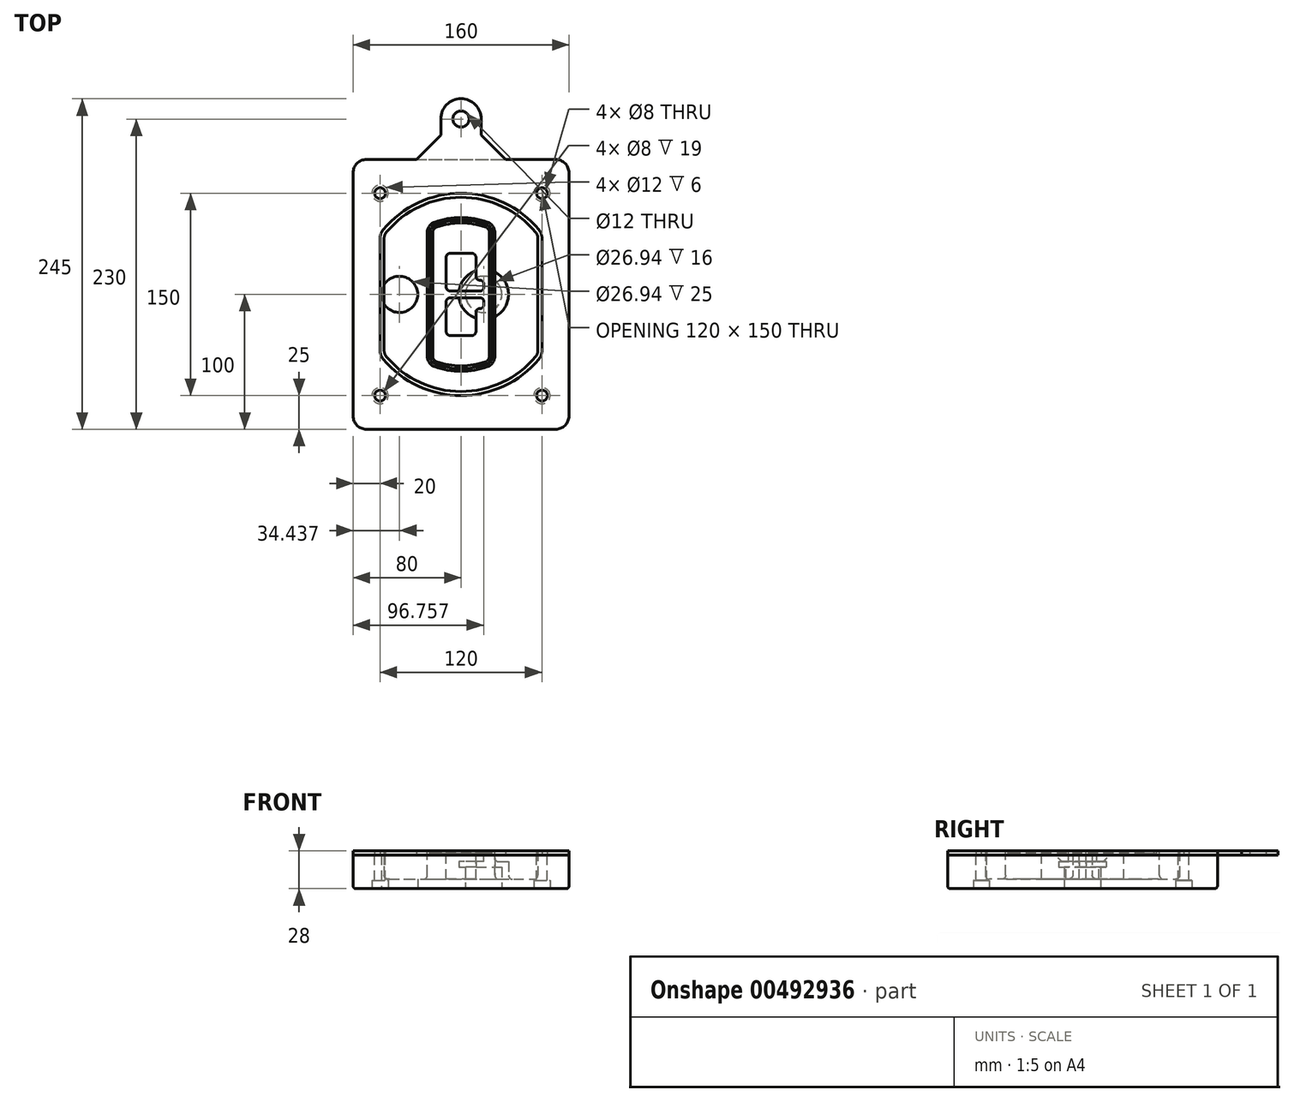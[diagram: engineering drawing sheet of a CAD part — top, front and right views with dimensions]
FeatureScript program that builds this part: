
annotation { "Feature Type Name" : "Feature", "Feature Type Description" : "" }
export const myFeature = defineFeature(function(context is Context, id is Id, definition is map)
    precondition{}
    {
        {
            var Q0;
            Q0=qCreatedBy(makeId("Top.planeOp"),FACE);
            var sketch = newSketch(context, id + "F0", { "sketchPlane" : qUnion([Q0])});
            skPoint(sketch, "E0.rect.middle", {"position": v(0, 0) * mm});
            skLineSegment(sketch, "E1.bottom", {"start": v(-70, -100) * mm, "end": v(70, -100) * mm});
            skLineSegment(sketch, "E1.top", {"start": v(-70, 100) * mm, "end": v(70, 100) * mm});
            skLineSegment(sketch, "E1.left", {"start": v(-80, -90) * mm, "end": v(-80, 90) * mm});
            skLineSegment(sketch, "E1.right", {"start": v(80, -90) * mm, "end": v(80, 90) * mm});
            skLineSegment(sketch, "E2", {"start": v(-80, 100) * mm, "end": v(80, -100) * mm, "construction": true});
            skLineSegment(sketch, "E3", {"start": v(80, 100) * mm, "end": v(-80, -100) * mm, "construction": true});
            skCircle(sketch, "E4", {"center": v(-60, 75) * mm, "radius": 4 * mm});
            skCircle(sketch, "E5", {"center": v(60, 75) * mm, "radius": 4 * mm});
            skCircle(sketch, "E6", {"center": v(60, -75) * mm, "radius": 4 * mm});
            skCircle(sketch, "E7", {"center": v(-60, -75) * mm, "radius": 4 * mm});
            skLineSegment(sketch, "E8", {"start": v(-60, 75) * mm, "end": v(60, 75) * mm, "construction": true});
            skLineSegment(sketch, "E9", {"start": v(60, 75) * mm, "end": v(60, -75) * mm, "construction": true});
            skLineSegment(sketch, "E10", {"start": v(60, -75) * mm, "end": v(-60, -75) * mm, "construction": true});
            skLineSegment(sketch, "E11", {"start": v(-60, -75) * mm, "end": v(-60, 75) * mm, "construction": true});
            skLineSegment(sketch, "E12", {"start": v(-60, 41.53) * mm, "end": v(-60, -41.53) * mm});
            skLineSegment(sketch, "E13", {"start": v(60, 41.53) * mm, "end": v(60, -41.53) * mm});
            skArc(sketch, "E14", {"start": v(57.7, 47.92) * mm, "mid": v(0, 75) * mm, "end": v(-57.7, 47.92) * mm});
            skArc(sketch, "E15", {"start": v(-57.7, -47.92) * mm, "mid": v(0, -75) * mm, "end": v(57.7, -47.92) * mm});
            skLineSegment(sketch, "E16", {"start": v(-60, 0) * mm, "end": v(60, 0) * mm, "construction": true});
            skPoint(sketch, "E17.visualSharp", {"position": v(-60, -45) * mm});
            skArc(sketch, "E17.filletArc", {"start": v(-60, -41.53) * mm, "mid": v(-59.4, -44.93) * mm, "end": v(-57.7, -47.92) * mm});
            skPoint(sketch, "E18.visualSharp", {"position": v(-60, 45) * mm});
            skArc(sketch, "E18.filletArc", {"start": v(-57.7, 47.92) * mm, "mid": v(-59.4, 44.93) * mm, "end": v(-60, 41.53) * mm});
            skPoint(sketch, "E19.visualSharp", {"position": v(60, 45) * mm});
            skArc(sketch, "E19.filletArc", {"start": v(60, 41.53) * mm, "mid": v(59.4, 44.93) * mm, "end": v(57.7, 47.92) * mm});
            skPoint(sketch, "E20.visualSharp", {"position": v(60, -45) * mm});
            skArc(sketch, "E20.filletArc", {"start": v(57.7, -47.92) * mm, "mid": v(59.4, -44.93) * mm, "end": v(60, -41.53) * mm});
            skPoint(sketch, "E21.visualSharp", {"position": v(-80, 100) * mm});
            skArc(sketch, "E21.filletArc", {"start": v(-70, 100) * mm, "mid": v(-77.07, 97.07) * mm, "end": v(-80, 90) * mm});
            skPoint(sketch, "E22.visualSharp", {"position": v(80, 100) * mm});
            skArc(sketch, "E22.filletArc", {"start": v(80, 90) * mm, "mid": v(77.07, 97.07) * mm, "end": v(70, 100) * mm});
            skPoint(sketch, "E23.visualSharp", {"position": v(80, -100) * mm});
            skArc(sketch, "E23.filletArc", {"start": v(70, -100) * mm, "mid": v(77.07, -97.07) * mm, "end": v(80, -90) * mm});
            skPoint(sketch, "E24.visualSharp", {"position": v(-80, -100) * mm});
            skArc(sketch, "E24.filletArc", {"start": v(-80, -90) * mm, "mid": v(-77.07, -97.07) * mm, "end": v(-70, -100) * mm});
            skArc(sketch, "E25.0", {"start": v(57, 41.53) * mm, "mid": v(56.58, 43.91) * mm, "end": v(55.38, 46) * mm});
            skLineSegment(sketch, "E25.1", {"start": v(57, 41.53) * mm, "end": v(57, -41.53) * mm});
            skArc(sketch, "E25.2", {"start": v(55.38, -46) * mm, "mid": v(56.58, -43.91) * mm, "end": v(57, -41.53) * mm});
            skArc(sketch, "E25.3", {"start": v(-55.38, -46) * mm, "mid": v(0, -72) * mm, "end": v(55.38, -46) * mm});
            skArc(sketch, "E25.4", {"start": v(-57, -41.53) * mm, "mid": v(-56.58, -43.91) * mm, "end": v(-55.38, -46) * mm});
            skArc(sketch, "E25.5", {"start": v(55.38, 46) * mm, "mid": v(0, 72) * mm, "end": v(-55.38, 46) * mm});
            skLineSegment(sketch, "E25.6", {"start": v(-57, 41.53) * mm, "end": v(-57, -41.53) * mm});
            skArc(sketch, "E25.7", {"start": v(-55.38, 46) * mm, "mid": v(-56.58, 43.91) * mm, "end": v(-57, 41.53) * mm});
            skArc(sketch, "E26.0", {"start": v(-60.77, 50.48) * mm, "mid": v(-63.17, 46.29) * mm, "end": v(-64, 41.53) * mm});
            skArc(sketch, "E26.1", {"start": v(60.77, 50.48) * mm, "mid": v(0, 79) * mm, "end": v(-60.77, 50.48) * mm});
            skArc(sketch, "E26.2", {"start": v(64, 41.53) * mm, "mid": v(63.17, 46.29) * mm, "end": v(60.77, 50.48) * mm});
            skLineSegment(sketch, "E26.3", {"start": v(64, 41.53) * mm, "end": v(64, -41.53) * mm});
            skArc(sketch, "E26.4", {"start": v(60.77, -50.48) * mm, "mid": v(63.17, -46.29) * mm, "end": v(64, -41.53) * mm});
            skLineSegment(sketch, "E26.5", {"start": v(-64, 41.53) * mm, "end": v(-64, -41.53) * mm});
            skArc(sketch, "E26.6", {"start": v(-60.77, -50.48) * mm, "mid": v(0, -79) * mm, "end": v(60.77, -50.48) * mm});
            skArc(sketch, "E26.7", {"start": v(-64, -41.53) * mm, "mid": v(-63.17, -46.29) * mm, "end": v(-60.77, -50.48) * mm});
            skSolve(sketch);
        }
        {
            var Q0;
            Q0=makeQuery(id+"F0.imprint","IMPRINT",FACE,{"disambiguationData":[TD([[makeQuery(id+"F0.imprint","IMPRINT",EDGE,{"derivedFrom":sQuery(id+"F0.wireOp",EDGE,"E1.bottom")}),1.0]])]});
            var Q1;
            Q1=makeQuery(id+"F0.imprint","IMPRINT",FACE,{"disambiguationData":[TD([[makeQuery(id+"F0.imprint","IMPRINT",EDGE,{"derivedFrom":sQuery(id+"F0.wireOp",EDGE,"E12")}),1.0]])]});
            var Q2;
            Q2=makeQuery(id+"F0.imprint","IMPRINT",FACE,{"disambiguationData":[TD([[makeQuery(id+"F0.imprint","IMPRINT",EDGE,{"derivedFrom":sQuery(id+"F0.wireOp",EDGE,"E25.0")}),1.0]])]});
            var Q3;
            Q3=makeQuery(id+"F0.imprint","IMPRINT",FACE,{"disambiguationData":[TD([[makeQuery(id+"F0.imprint","IMPRINT",EDGE,{"derivedFrom":sQuery(id+"F0.wireOp",EDGE,"E12")}),-1.0]])]});
            extrude(context, id + "F1", {"entities" : qUnion([Q0, Q1, Q2, Q3]), "oppositeDirection" : true, "depth" : 25 * mm});
        }
        {
            var Q0;
            Q0=makeQuery(id+"F0.imprint","IMPRINT",FACE,{"disambiguationData":[TD([[makeQuery(id+"F0.imprint","IMPRINT",EDGE,{"derivedFrom":sQuery(id+"F0.wireOp",EDGE,"E12")}),1.0]])]});
            extrude(context, id + "F2", {"entities" : qUnion([Q0]), "operationType" : NewBodyOperationType.ADD, "depth" : 3 * mm});
        }
        {
            var Q0;
            Q0=makeQuery(id+"F0.imprint","IMPRINT",FACE,{"disambiguationData":[TD([[makeQuery(id+"F0.imprint","IMPRINT",EDGE,{"derivedFrom":sQuery(id+"F0.wireOp",EDGE,"E25.0")}),1.0]])]});
            extrude(context, id + "F3", {"entities" : qUnion([Q0]), "operationType" : NewBodyOperationType.REMOVE, "oppositeDirection" : true, "depth" : 18 * mm});
        }
        {
            var Q0;
            Q0=makeQuery(id+"F2.opExtrude","CAP_FACE",FACE,{"disambiguationData":[OSD([sQuery(id+"F0.wireOp",EDGE,"E12"),sQuery(id+"F0.wireOp",EDGE,"E13"),sQuery(id+"F0.wireOp",EDGE,"E14"),sQuery(id+"F0.wireOp",EDGE,"E15"),sQuery(id+"F0.wireOp",EDGE,"E17.filletArc"),sQuery(id+"F0.wireOp",EDGE,"E18.filletArc"),sQuery(id+"F0.wireOp",EDGE,"E19.filletArc"),sQuery(id+"F0.wireOp",EDGE,"E20.filletArc"),sQuery(id+"F0.wireOp",EDGE,"E25.0"),sQuery(id+"F0.wireOp",EDGE,"E25.1"),sQuery(id+"F0.wireOp",EDGE,"E25.2"),sQuery(id+"F0.wireOp",EDGE,"E25.3"),sQuery(id+"F0.wireOp",EDGE,"E25.4"),sQuery(id+"F0.wireOp",EDGE,"E25.5"),sQuery(id+"F0.wireOp",EDGE,"E25.6"),sQuery(id+"F0.wireOp",EDGE,"E25.7")])],"isStart":false});
            var sketch = newSketch(context, id + "F4", { "sketchPlane" : qUnion([Q0])});
            skArc(sketch, "E27.0", {"start": v(-19.78, -53.46) * mm, "mid": v(0, -57) * mm, "end": v(19.78, -53.46) * mm});
            skArc(sketch, "E28.0", {"start": v(19.78, 53.46) * mm, "mid": v(0, 57) * mm, "end": v(-19.78, 53.46) * mm});
            skLineSegment(sketch, "E29", {"start": v(-25, 45.96) * mm, "end": v(-25, -45.96) * mm});
            skLineSegment(sketch, "E30", {"start": v(25, 45.96) * mm, "end": v(25, -45.96) * mm});
            skLineSegment(sketch, "E31", {"start": v(-25, 51.22) * mm, "end": v(25, 51.22) * mm, "construction": true});
            skLineSegment(sketch, "E32", {"start": v(-25, -51.22) * mm, "end": v(25, -51.22) * mm, "construction": true});
            skPoint(sketch, "E33.visualSharp", {"position": v(-25, 51.22) * mm});
            skArc(sketch, "E33.filletArc", {"start": v(-19.78, 53.46) * mm, "mid": v(-23.57, 50.53) * mm, "end": v(-25, 45.96) * mm});
            skPoint(sketch, "E34.visualSharp", {"position": v(25, 51.22) * mm});
            skArc(sketch, "E34.filletArc", {"start": v(25, 45.96) * mm, "mid": v(23.57, 50.53) * mm, "end": v(19.78, 53.46) * mm});
            skPoint(sketch, "E35.visualSharp", {"position": v(25, -51.22) * mm});
            skArc(sketch, "E35.filletArc", {"start": v(19.78, -53.46) * mm, "mid": v(23.57, -50.53) * mm, "end": v(25, -45.96) * mm});
            skPoint(sketch, "E36.visualSharp", {"position": v(-25, -51.22) * mm});
            skArc(sketch, "E36.filletArc", {"start": v(-25, -45.96) * mm, "mid": v(-23.57, -50.53) * mm, "end": v(-19.78, -53.46) * mm});
            skArc(sketch, "E37.0", {"start": v(55.38, 46) * mm, "mid": v(0, 72) * mm, "end": v(-55.38, 46) * mm});
            skArc(sketch, "E37.1", {"start": v(-55.38, 46) * mm, "mid": v(-56.58, 43.91) * mm, "end": v(-57, 41.53) * mm});
            skLineSegment(sketch, "E37.2", {"start": v(-57, 41.53) * mm, "end": v(-57, -41.53) * mm});
            skArc(sketch, "E37.3", {"start": v(-57, -41.53) * mm, "mid": v(-56.58, -43.91) * mm, "end": v(-55.38, -46) * mm});
            skArc(sketch, "E37.4", {"start": v(-55.38, -46) * mm, "mid": v(0, -72) * mm, "end": v(55.38, -46) * mm});
            skArc(sketch, "E37.5", {"start": v(55.38, -46) * mm, "mid": v(56.58, -43.91) * mm, "end": v(57, -41.53) * mm});
            skLineSegment(sketch, "E37.6", {"start": v(57, 41.53) * mm, "end": v(57, -41.53) * mm});
            skArc(sketch, "E37.7", {"start": v(57, 41.53) * mm, "mid": v(56.58, 43.91) * mm, "end": v(55.38, 46) * mm});
            skLineSegment(sketch, "E38.0", {"start": v(23, 45.96) * mm, "end": v(23, -45.96) * mm});
            skArc(sketch, "E38.1", {"start": v(19.08, -51.58) * mm, "mid": v(21.92, -49.39) * mm, "end": v(23, -45.96) * mm});
            skArc(sketch, "E38.2", {"start": v(-19.08, -51.58) * mm, "mid": v(0, -55) * mm, "end": v(19.08, -51.58) * mm});
            skArc(sketch, "E38.3", {"start": v(-23, -45.96) * mm, "mid": v(-21.92, -49.39) * mm, "end": v(-19.08, -51.58) * mm});
            skLineSegment(sketch, "E38.4", {"start": v(-23, 45.96) * mm, "end": v(-23, -45.96) * mm});
            skArc(sketch, "E38.5", {"start": v(23, 45.96) * mm, "mid": v(21.92, 49.39) * mm, "end": v(19.08, 51.58) * mm});
            skArc(sketch, "E38.6", {"start": v(-19.08, 51.58) * mm, "mid": v(-21.92, 49.39) * mm, "end": v(-23, 45.96) * mm});
            skArc(sketch, "E38.7", {"start": v(19.08, 51.58) * mm, "mid": v(0, 55) * mm, "end": v(-19.08, 51.58) * mm});
            skArc(sketch, "E39.0", {"start": v(21, 45.96) * mm, "mid": v(20.28, 48.24) * mm, "end": v(18.39, 49.7) * mm});
            skLineSegment(sketch, "E39.1", {"start": v(21, 45.96) * mm, "end": v(21, -45.96) * mm});
            skArc(sketch, "E39.2", {"start": v(18.39, -49.7) * mm, "mid": v(20.28, -48.24) * mm, "end": v(21, -45.96) * mm});
            skArc(sketch, "E39.3", {"start": v(-18.39, -49.7) * mm, "mid": v(0, -53) * mm, "end": v(18.39, -49.7) * mm});
            skArc(sketch, "E39.4", {"start": v(-21, -45.96) * mm, "mid": v(-20.28, -48.24) * mm, "end": v(-18.39, -49.7) * mm});
            skArc(sketch, "E39.5", {"start": v(18.39, 49.7) * mm, "mid": v(0, 53) * mm, "end": v(-18.39, 49.7) * mm});
            skLineSegment(sketch, "E39.6", {"start": v(-21, 45.96) * mm, "end": v(-21, -45.96) * mm});
            skArc(sketch, "E39.7", {"start": v(-18.39, 49.7) * mm, "mid": v(-20.28, 48.24) * mm, "end": v(-21, 45.96) * mm});
            skLineSegment(sketch, "E40", {"start": v(-25, 0) * mm, "end": v(25, 0) * mm, "construction": true});
            skLineSegment(sketch, "E41", {"start": v(-11, 5.5) * mm, "end": v(-11, 27.5) * mm});
            skLineSegment(sketch, "E42", {"start": v(-8, 30.5) * mm, "end": v(8, 30.5) * mm});
            skLineSegment(sketch, "E43", {"start": v(11, 27.5) * mm, "end": v(11, 13.5) * mm});
            skLineSegment(sketch, "E44", {"start": v(14, 10.5) * mm, "end": v(14, 10.5) * mm});
            skLineSegment(sketch, "E45", {"start": v(17, 7.5) * mm, "end": v(17, 5.5) * mm});
            skLineSegment(sketch, "E46", {"start": v(14, 2.5) * mm, "end": v(-8, 2.5) * mm});
            skPoint(sketch, "E47.visualSharp", {"position": v(-11, 30.5) * mm});
            skArc(sketch, "E47.filletArc", {"start": v(-8, 30.5) * mm, "mid": v(-10.12, 29.62) * mm, "end": v(-11, 27.5) * mm});
            skPoint(sketch, "E48.visualSharp", {"position": v(11, 30.5) * mm});
            skArc(sketch, "E48.filletArc", {"start": v(11, 27.5) * mm, "mid": v(10.12, 29.62) * mm, "end": v(8, 30.5) * mm});
            skPoint(sketch, "E49.visualSharp", {"position": v(11, 10.5) * mm});
            skArc(sketch, "E49.filletArc", {"start": v(11, 13.5) * mm, "mid": v(11.88, 11.38) * mm, "end": v(14, 10.5) * mm});
            skPoint(sketch, "E50.visualSharp", {"position": v(17, 10.5) * mm});
            skArc(sketch, "E50.filletArc", {"start": v(17, 7.5) * mm, "mid": v(16.12, 9.62) * mm, "end": v(14, 10.5) * mm});
            skPoint(sketch, "E51.visualSharp", {"position": v(17, 2.5) * mm});
            skArc(sketch, "E51.filletArc", {"start": v(14, 2.5) * mm, "mid": v(16.12, 3.38) * mm, "end": v(17, 5.5) * mm});
            skPoint(sketch, "E52.visualSharp", {"position": v(-11, 2.5) * mm});
            skArc(sketch, "E52.filletArc", {"start": v(-11, 5.5) * mm, "mid": v(-10.12, 3.38) * mm, "end": v(-8, 2.5) * mm});
            skLineSegment(sketch, "E53.0.MirrorCS", {"start": v(14, -2.5) * mm, "end": v(-8, -2.5) * mm});
            skArc(sketch, "E54.0.MirrorCS", {"start": v(-11, -5.5) * mm, "mid": v(-10.12, -3.38) * mm, "end": v(-8, -2.5) * mm});
            skLineSegment(sketch, "E55.0.MirrorCS", {"start": v(-11, -5.5) * mm, "end": v(-11, -27.5) * mm});
            skArc(sketch, "E56.0.MirrorCS", {"start": v(-8, -30.5) * mm, "mid": v(-10.12, -29.62) * mm, "end": v(-11, -27.5) * mm});
            skLineSegment(sketch, "E57.0.MirrorCS", {"start": v(-8, -30.5) * mm, "end": v(8, -30.5) * mm});
            skArc(sketch, "E58.0.MirrorCS", {"start": v(11, -27.5) * mm, "mid": v(10.12, -29.62) * mm, "end": v(8, -30.5) * mm});
            skLineSegment(sketch, "E59.0.MirrorCS", {"start": v(11, -27.5) * mm, "end": v(11, -13.5) * mm});
            skArc(sketch, "E60.0.MirrorCS", {"start": v(11, -13.5) * mm, "mid": v(11.88, -11.38) * mm, "end": v(14, -10.5) * mm});
            skArc(sketch, "E61.0.MirrorCS", {"start": v(17, -7.5) * mm, "mid": v(16.12, -9.62) * mm, "end": v(14, -10.5) * mm});
            skLineSegment(sketch, "E62.0.MirrorCS", {"start": v(17, -7.5) * mm, "end": v(17, -5.5) * mm});
            skArc(sketch, "E63.0.MirrorCS", {"start": v(14, -2.5) * mm, "mid": v(16.12, -3.38) * mm, "end": v(17, -5.5) * mm});
            skSolve(sketch);
        }
        {
            var Q0;
            Q0=makeQuery(id+"F4.imprint","IMPRINT",FACE,{"disambiguationData":[TD([[makeQuery(id+"F4.imprint","IMPRINT",EDGE,{"derivedFrom":sQuery(id+"F4.wireOp",EDGE,"E27.0")}),1.0]])]});
            var Q1;
            Q1=makeQuery(id+"F4.imprint","IMPRINT",FACE,{"disambiguationData":[TD([[makeQuery(id+"F4.imprint","IMPRINT",EDGE,{"derivedFrom":sQuery(id+"F4.wireOp",EDGE,"E38.0")}),-1.0]])]});
            var Q2;
            Q2=makeQuery(id+"F4.imprint","IMPRINT",FACE,{"disambiguationData":[TD([[makeQuery(id+"F4.imprint","IMPRINT",EDGE,{"derivedFrom":sQuery(id+"F4.wireOp",EDGE,"E39.0")}),1.0]])]});
            extrude(context, id + "F5", {"entities" : qUnion([Q0, Q1, Q2]), "operationType" : NewBodyOperationType.ADD, "endBound" : BoundingType.UP_TO_NEXT, "oppositeDirection" : true, "depth" : 25 * mm});
        }
        {
            var Q0;
            Q0=makeQuery(id+"F4.imprint","IMPRINT",FACE,{"disambiguationData":[TD([[makeQuery(id+"F4.imprint","IMPRINT",EDGE,{"derivedFrom":sQuery(id+"F4.wireOp",EDGE,"E38.0")}),-1.0]])]});
            extrude(context, id + "F6", {"entities" : qUnion([Q0]), "operationType" : NewBodyOperationType.REMOVE, "oppositeDirection" : true, "depth" : 2 * mm});
        }
        {
            var Q0;
            Q0=makeQuery(id+"F1.opExtrude","CAP_FACE",FACE,{"disambiguationData":[OSD([sQuery(id+"F0.wireOp",EDGE,"E1.bottom"),sQuery(id+"F0.wireOp",EDGE,"E1.top"),sQuery(id+"F0.wireOp",EDGE,"E1.left"),sQuery(id+"F0.wireOp",EDGE,"E1.right"),sQuery(id+"F0.wireOp",EDGE,"E4"),sQuery(id+"F0.wireOp",EDGE,"E5"),sQuery(id+"F0.wireOp",EDGE,"E6"),sQuery(id+"F0.wireOp",EDGE,"E7"),sQuery(id+"F0.wireOp",EDGE,"E21.filletArc"),sQuery(id+"F0.wireOp",EDGE,"E22.filletArc"),sQuery(id+"F0.wireOp",EDGE,"E23.filletArc"),sQuery(id+"F0.wireOp",EDGE,"E24.filletArc")])],"isStart":false});
            var sketch = newSketch(context, id + "F7", { "sketchPlane" : qUnion([Q0])});
            skCircle(sketch, "E64", {"center": v(16.76, 0) * mm, "radius": 13.47 * mm});
            skCircle(sketch, "E65", {"center": v(-45.56, 0) * mm, "radius": 13.47 * mm});
            skLineSegment(sketch, "E66", {"start": v(80, 0) * mm, "end": v(-80, 0) * mm});
            skCircle(sketch, "E67", {"center": v(16.76, 0) * mm, "radius": 18.47 * mm});
            skCircle(sketch, "E68", {"center": v(60, -75) * mm, "radius": 6 * mm});
            skCircle(sketch, "E69", {"center": v(-60, -75) * mm, "radius": 6 * mm});
            skCircle(sketch, "E70", {"center": v(-60, 75) * mm, "radius": 6 * mm});
            skCircle(sketch, "E71", {"center": v(60, 75) * mm, "radius": 6 * mm});
            skSolve(sketch);
        }
        {
            var Q0;
            {var subQ1=sQuery(id+"F7.wireOp",EDGE,"E66");var subQ4=sQuery(id+"F7.wireOp",EDGE,"E64");var subQ6=makeQuery(id+"F7.imprint","INTERSECT",VERTEX,{"disambiguationData":[OD(0.0)],"derivedFrom":[subQ4,subQ1]});Q0=makeQuery(id+"F7.imprint","IMPRINT",FACE,{"disambiguationData":[TD([[makeQuery(id+"F7.imprint","IMPRINT",EDGE,{"disambiguationData":[TD([[subQ6,-1.0]])],"derivedFrom":subQ4}),-1.0]])]});}
            var Q1;
            {var subQ0=sQuery(id+"F7.wireOp",EDGE,"E66");var subQ1=sQuery(id+"F7.wireOp",EDGE,"E64");var subQ3=makeQuery(id+"F7.imprint","INTERSECT",VERTEX,{"disambiguationData":[OD(0.0)],"derivedFrom":[subQ1,subQ0]});Q1=makeQuery(id+"F7.imprint","IMPRINT",FACE,{"disambiguationData":[TD([[makeQuery(id+"F7.imprint","IMPRINT",EDGE,{"disambiguationData":[TD([[subQ3,-1.0]])],"derivedFrom":subQ1}),1.0]])]});}
            var Q2;
            {var subQ0=sQuery(id+"F7.wireOp",EDGE,"E66");var subQ1=sQuery(id+"F7.wireOp",EDGE,"E64");var subQ3=makeQuery(id+"F7.imprint","INTERSECT",VERTEX,{"disambiguationData":[OD(0.0)],"derivedFrom":[subQ1,subQ0]});Q2=makeQuery(id+"F7.imprint","IMPRINT",FACE,{"disambiguationData":[TD([[makeQuery(id+"F7.imprint","IMPRINT",EDGE,{"disambiguationData":[TD([[subQ3,1.0]])],"derivedFrom":subQ1}),1.0]])]});}
            var Q3;
            {var subQ1=sQuery(id+"F7.wireOp",EDGE,"E66");var subQ4=sQuery(id+"F7.wireOp",EDGE,"E64");var subQ6=makeQuery(id+"F7.imprint","INTERSECT",VERTEX,{"disambiguationData":[OD(0.0)],"derivedFrom":[subQ4,subQ1]});Q3=makeQuery(id+"F7.imprint","IMPRINT",FACE,{"disambiguationData":[TD([[makeQuery(id+"F7.imprint","IMPRINT",EDGE,{"disambiguationData":[TD([[subQ6,1.0]])],"derivedFrom":subQ4}),-1.0]])]});}
            extrude(context, id + "F8", {"entities" : qUnion([Q0, Q1, Q2, Q3]), "operationType" : NewBodyOperationType.ADD, "oppositeDirection" : true, "depth" : 20 * mm});
        }
        {
            var Q0;
            {var subQ0=sQuery(id+"F7.wireOp",EDGE,"E66");var subQ1=sQuery(id+"F7.wireOp",EDGE,"E64");var subQ3=makeQuery(id+"F7.imprint","INTERSECT",VERTEX,{"disambiguationData":[OD(0.0)],"derivedFrom":[subQ1,subQ0]});Q0=makeQuery(id+"F7.imprint","IMPRINT",FACE,{"disambiguationData":[TD([[makeQuery(id+"F7.imprint","IMPRINT",EDGE,{"disambiguationData":[TD([[subQ3,-1.0]])],"derivedFrom":subQ1}),1.0]])]});}
            var Q1;
            {var subQ0=sQuery(id+"F7.wireOp",EDGE,"E66");var subQ1=sQuery(id+"F7.wireOp",EDGE,"E64");var subQ3=makeQuery(id+"F7.imprint","INTERSECT",VERTEX,{"disambiguationData":[OD(0.0)],"derivedFrom":[subQ1,subQ0]});Q1=makeQuery(id+"F7.imprint","IMPRINT",FACE,{"disambiguationData":[TD([[makeQuery(id+"F7.imprint","IMPRINT",EDGE,{"disambiguationData":[TD([[subQ3,1.0]])],"derivedFrom":subQ1}),1.0]])]});}
            extrude(context, id + "F9", {"entities" : qUnion([Q0, Q1]), "operationType" : NewBodyOperationType.REMOVE, "oppositeDirection" : true, "depth" : 16 * mm});
        }
        {
            var Q0;
            {var subQ0=sQuery(id+"F7.wireOp",EDGE,"E66");var subQ1=sQuery(id+"F7.wireOp",EDGE,"E65");var subQ3=makeQuery(id+"F7.imprint","INTERSECT",VERTEX,{"disambiguationData":[OD(0.0)],"derivedFrom":[subQ1,subQ0]});Q0=makeQuery(id+"F7.imprint","IMPRINT",FACE,{"disambiguationData":[TD([[makeQuery(id+"F7.imprint","IMPRINT",EDGE,{"disambiguationData":[TD([[subQ3,-1.0]])],"derivedFrom":subQ1}),1.0]])]});}
            var Q1;
            {var subQ0=sQuery(id+"F7.wireOp",EDGE,"E66");var subQ1=sQuery(id+"F7.wireOp",EDGE,"E65");var subQ3=makeQuery(id+"F7.imprint","INTERSECT",VERTEX,{"disambiguationData":[OD(0.0)],"derivedFrom":[subQ1,subQ0]});Q1=makeQuery(id+"F7.imprint","IMPRINT",FACE,{"disambiguationData":[TD([[makeQuery(id+"F7.imprint","IMPRINT",EDGE,{"disambiguationData":[TD([[subQ3,1.0]])],"derivedFrom":subQ1}),1.0]])]});}
            extrude(context, id + "F10", {"entities" : qUnion([Q0, Q1]), "operationType" : NewBodyOperationType.REMOVE, "oppositeDirection" : true, "depth" : 25 * mm});
        }
        {
            var Q0;
            Q0=makeQuery(id+"F7.imprint","IMPRINT",FACE,{"disambiguationData":[TD([[makeQuery(id+"F7.imprint","IMPRINT",EDGE,{"derivedFrom":sQuery(id+"F7.wireOp",EDGE,"E68")}),1.0]])]});
            var Q1;
            Q1=makeQuery(id+"F7.imprint","IMPRINT",FACE,{"disambiguationData":[TD([[makeQuery(id+"F7.imprint","IMPRINT",EDGE,{"derivedFrom":makeQuery(id+"F1.opExtrude","CAP_EDGE",EDGE,{"disambiguationData":[OSD([sQuery(id+"F0.wireOp",EDGE,"E5")])],"isStart":false})}),-1.0]])]});
            var Q2;
            Q2=makeQuery(id+"F7.imprint","IMPRINT",FACE,{"disambiguationData":[TD([[makeQuery(id+"F7.imprint","IMPRINT",EDGE,{"derivedFrom":sQuery(id+"F7.wireOp",EDGE,"E69")}),1.0]])]});
            var Q3;
            Q3=makeQuery(id+"F7.imprint","IMPRINT",FACE,{"disambiguationData":[TD([[makeQuery(id+"F7.imprint","IMPRINT",EDGE,{"derivedFrom":makeQuery(id+"F1.opExtrude","CAP_EDGE",EDGE,{"disambiguationData":[OSD([sQuery(id+"F0.wireOp",EDGE,"E4")])],"isStart":false})}),-1.0]])]});
            var Q4;
            Q4=makeQuery(id+"F7.imprint","IMPRINT",FACE,{"disambiguationData":[TD([[makeQuery(id+"F7.imprint","IMPRINT",EDGE,{"derivedFrom":sQuery(id+"F7.wireOp",EDGE,"E70")}),1.0]])]});
            var Q5;
            Q5=makeQuery(id+"F7.imprint","IMPRINT",FACE,{"disambiguationData":[TD([[makeQuery(id+"F7.imprint","IMPRINT",EDGE,{"derivedFrom":makeQuery(id+"F1.opExtrude","CAP_EDGE",EDGE,{"disambiguationData":[OSD([sQuery(id+"F0.wireOp",EDGE,"E7")])],"isStart":false})}),-1.0]])]});
            var Q6;
            Q6=makeQuery(id+"F7.imprint","IMPRINT",FACE,{"disambiguationData":[TD([[makeQuery(id+"F7.imprint","IMPRINT",EDGE,{"derivedFrom":sQuery(id+"F7.wireOp",EDGE,"E71")}),1.0]])]});
            var Q7;
            Q7=makeQuery(id+"F7.imprint","IMPRINT",FACE,{"disambiguationData":[TD([[makeQuery(id+"F7.imprint","IMPRINT",EDGE,{"derivedFrom":makeQuery(id+"F1.opExtrude","CAP_EDGE",EDGE,{"disambiguationData":[OSD([sQuery(id+"F0.wireOp",EDGE,"E6")])],"isStart":false})}),-1.0]])]});
            extrude(context, id + "F11", {"entities" : qUnion([Q0, Q1, Q2, Q3, Q4, Q5, Q6, Q7]), "operationType" : NewBodyOperationType.REMOVE, "oppositeDirection" : true, "depth" : 6 * mm});
        }
        {
            var Q0;
            Q0=makeQuery(id+"F9.boolean.opBoolean","COPY",FACE,{"derivedFrom":makeQuery(id+"F9.opExtrude","CAP_FACE",FACE,{"disambiguationData":[OSD([sQuery(id+"F7.wireOp",EDGE,"E64")])],"isStart":false})});
            var sketch = newSketch(context, id + "F12", { "sketchPlane" : qUnion([Q0])});
            skArc(sketch, "E72.0", {"start": v(11, 17.55) * mm, "mid": v(2.57, 11.82) * mm, "end": v(-1.54, 2.5) * mm});
            skArc(sketch, "E72.1", {"start": v(-1.54, -2.5) * mm, "mid": v(2.57, -11.82) * mm, "end": v(11, -17.55) * mm});
            skLineSegment(sketch, "E73", {"start": v(-1.54, -2.5) * mm, "end": v(14, -2.5) * mm});
            skLineSegment(sketch, "E74.0", {"start": v(14, 2.5) * mm, "end": v(-1.54, 2.5) * mm});
            skArc(sketch, "E74.1", {"start": v(14, 2.5) * mm, "mid": v(16.12, 3.38) * mm, "end": v(17, 5.5) * mm});
            skLineSegment(sketch, "E74.2", {"start": v(17, 7.5) * mm, "end": v(17, 5.5) * mm});
            skArc(sketch, "E74.3", {"start": v(17, 7.5) * mm, "mid": v(16.12, 9.62) * mm, "end": v(14, 10.5) * mm});
            skArc(sketch, "E74.4", {"start": v(11, 13.5) * mm, "mid": v(11.88, 11.38) * mm, "end": v(14, 10.5) * mm});
            skLineSegment(sketch, "E74.5", {"start": v(11, 17.55) * mm, "end": v(11, 13.5) * mm});
            skLineSegment(sketch, "E74.7", {"start": v(14, -2.5) * mm, "end": v(-1.54, -2.5) * mm});
            skArc(sketch, "E74.8", {"start": v(14, -2.5) * mm, "mid": v(16.12, -3.38) * mm, "end": v(17, -5.5) * mm});
            skLineSegment(sketch, "E74.9", {"start": v(17, -7.5) * mm, "end": v(17, -5.5) * mm});
            skArc(sketch, "E74.10", {"start": v(17, -7.5) * mm, "mid": v(16.12, -9.62) * mm, "end": v(14, -10.5) * mm});
            skArc(sketch, "E74.11", {"start": v(11, -13.5) * mm, "mid": v(11.88, -11.38) * mm, "end": v(14, -10.5) * mm});
            skLineSegment(sketch, "E74.12", {"start": v(11, -17.55) * mm, "end": v(11, -13.5) * mm});
            skPoint(sketch, "E75.orphan", {"position": v(11, -27.5) * mm});
            skPoint(sketch, "E76.orphan", {"position": v(-8, -2.5) * mm});
            skPoint(sketch, "E77.orphan", {"position": v(-8, 2.5) * mm});
            skPoint(sketch, "E78.orphan", {"position": v(11, 27.5) * mm});
            skSolve(sketch);
        }
        {
            var Q0;
            {var subQ7=sQuery(id+"F12.wireOp",EDGE,"E72.0");var subQ14=sQuery(id+"F12.wireOp",EDGE,"E72.1");var subQ16=sQuery(id+"F12.wireOp",EDGE,"E74.1");var subQ18=sQuery(id+"F12.wireOp",EDGE,"E74.8");Q0=qUnion([makeQuery(id+"F12.imprint","IMPRINT",FACE,{"disambiguationData":[TD([[makeQuery(id+"F12.imprint","IMPRINT",EDGE,{"derivedFrom":subQ7}),1.0]])]}),makeQuery(id+"F12.imprint","IMPRINT",FACE,{"disambiguationData":[TD([[makeQuery(id+"F12.imprint","IMPRINT",EDGE,{"derivedFrom":subQ14}),1.0]])]}),makeQuery(id+"F12.imprint","IMPRINT",FACE,{"disambiguationData":[TD([[makeQuery(id+"F12.imprint","IMPRINT",EDGE,{"derivedFrom":subQ16}),1.0]])]}),makeQuery(id+"F12.imprint","IMPRINT",FACE,{"disambiguationData":[TD([[makeQuery(id+"F12.imprint","IMPRINT",EDGE,{"derivedFrom":subQ18}),-1.0]])]})]);}
            var Q1;
            Q1=makeQuery(id+"F5.boolean.opBoolean","SPLIT",FACE,{"disambiguationData":[TD([makeQuery(id+"F5.opExtrude","SWEPT_FACE",FACE,{"disambiguationData":[OSD([sQuery(id+"F4.wireOp",EDGE,"E41")])]})])],"derivedFrom":makeQuery(id+"F3.boolean.opBoolean","COPY",FACE,{"derivedFrom":makeQuery(id+"F3.opExtrude","CAP_FACE",FACE,{"disambiguationData":[OSD([sQuery(id+"F0.wireOp",EDGE,"E25.0"),sQuery(id+"F0.wireOp",EDGE,"E25.1"),sQuery(id+"F0.wireOp",EDGE,"E25.2"),sQuery(id+"F0.wireOp",EDGE,"E25.3"),sQuery(id+"F0.wireOp",EDGE,"E25.4"),sQuery(id+"F0.wireOp",EDGE,"E25.5"),sQuery(id+"F0.wireOp",EDGE,"E25.6"),sQuery(id+"F0.wireOp",EDGE,"E25.7")])],"isStart":false})})});
            extrude(context, id + "F13", {"entities" : qUnion([Q0]), "operationType" : NewBodyOperationType.REMOVE, "endBound" : BoundingType.UP_TO_SURFACE, "endBoundEntityFace" : qUnion([Q1]), "depth" : 25 * mm});
        }
        {
            var Q0;
            Q0=makeQuery(id+"F3.boolean.opBoolean","COPY",EDGE,{"derivedFrom":makeQuery(id+"F3.opExtrude","CAP_EDGE",EDGE,{"disambiguationData":[OSD([sQuery(id+"F0.wireOp",EDGE,"E25.6")])],"isStart":false})});
            var Q1;
            Q1=makeQuery(id+"F8.boolean.opBoolean","INTERSECT",EDGE,{"derivedFrom":[makeQuery(id+"F5.opExtrude","SWEPT_FACE",FACE,{"disambiguationData":[OSD([sQuery(id+"F4.wireOp",EDGE,"E30")])]}),makeQuery(id+"F8.opExtrude","CAP_FACE",FACE,{"disambiguationData":[OSD([sQuery(id+"F7.wireOp",EDGE,"E67")])],"isStart":false})]});
            var Q2;
            Q2=makeQuery(id+"F8.boolean.opBoolean","INTERSECT",EDGE,{"disambiguationData":[OD(1.0)],"derivedFrom":[makeQuery(id+"F5.opExtrude","SWEPT_FACE",FACE,{"disambiguationData":[OSD([sQuery(id+"F4.wireOp",EDGE,"E30")])]}),makeQuery(id+"F8.opExtrude","SWEPT_FACE",FACE,{"disambiguationData":[OSD([sQuery(id+"F7.wireOp",EDGE,"E67")])]})]});
            var Q3;
            {var subQ0=sQuery(id+"F4.wireOp",EDGE,"E30");Q3=makeQuery(id+"F8.boolean.opBoolean","SPLIT",EDGE,{"disambiguationData":[TD([makeQuery(id+"F5.opExtrude","SWEPT_FACE",FACE,{"disambiguationData":[OSD([sQuery(id+"F4.wireOp",EDGE,"E35.filletArc")])]})])],"derivedFrom":makeQuery(id+"F5.opExtrude","CAP_EDGE",EDGE,{"disambiguationData":[OSD([subQ0])],"isStart":false})});}
            var Q4;
            {var subQ0=sQuery(id+"F0.wireOp",EDGE,"E25.7");var subQ1=sQuery(id+"F0.wireOp",EDGE,"E25.1");var subQ2=sQuery(id+"F0.wireOp",EDGE,"E25.6");var subQ3=sQuery(id+"F0.wireOp",EDGE,"E25.5");var subQ4=sQuery(id+"F0.wireOp",EDGE,"E25.4");var subQ5=sQuery(id+"F0.wireOp",EDGE,"E25.0");var subQ6=sQuery(id+"F0.wireOp",EDGE,"E25.2");var subQ7=sQuery(id+"F0.wireOp",EDGE,"E25.3");Q4=makeQuery(id+"F8.boolean.opBoolean","INTERSECT",EDGE,{"derivedFrom":[makeQuery(id+"F5.boolean.opBoolean","SPLIT",FACE,{"disambiguationData":[TD([makeQuery(id+"F2.opExtrude","SWEPT_FACE",FACE,{"disambiguationData":[OSD([subQ5])]})])],"derivedFrom":makeQuery(id+"F3.boolean.opBoolean","COPY",FACE,{"derivedFrom":makeQuery(id+"F3.opExtrude","CAP_FACE",FACE,{"disambiguationData":[OSD([subQ5,subQ1,subQ6,subQ7,subQ4,subQ3,subQ2,subQ0])],"isStart":false})})}),makeQuery(id+"F8.opExtrude","SWEPT_FACE",FACE,{"disambiguationData":[OSD([sQuery(id+"F7.wireOp",EDGE,"E67")])]})]});}
            var Q5;
            Q5=makeQuery(id+"F8.boolean.opBoolean","INTERSECT",EDGE,{"disambiguationData":[OD(0.0)],"derivedFrom":[makeQuery(id+"F5.opExtrude","SWEPT_FACE",FACE,{"disambiguationData":[OSD([sQuery(id+"F4.wireOp",EDGE,"E30")])]}),makeQuery(id+"F8.opExtrude","SWEPT_FACE",FACE,{"disambiguationData":[OSD([sQuery(id+"F7.wireOp",EDGE,"E67")])]})]});
            fillet(context, id + "F14", {"entities" : qUnion([Q0, Q1, Q2, Q3, Q4, Q5]), "radius" : 3 * mm, "tangentPropagation" : true, "allowEdgeOverflow" : false});
        }
        {
            var Q0;
            Q0=makeQuery(id+"F1.opExtrude","CAP_EDGE",EDGE,{"disambiguationData":[OSD([sQuery(id+"F0.wireOp",EDGE,"E1.bottom")])],"isStart":false});
            fillet(context, id + "F15", {"entities" : qUnion([Q0]), "radius" : 2 * mm, "tangentPropagation" : true, "allowEdgeOverflow" : false});
        }
        {
            var Q0;
            {var subQ0=sQuery(id+"F0.wireOp",EDGE,"E21.filletArc");var subQ1=sQuery(id+"F0.wireOp",EDGE,"E7");var subQ2=sQuery(id+"F0.wireOp",EDGE,"E6");var subQ3=sQuery(id+"F0.wireOp",EDGE,"E5");var subQ4=sQuery(id+"F0.wireOp",EDGE,"E4");var subQ5=sQuery(id+"F0.wireOp",EDGE,"E22.filletArc");var subQ6=sQuery(id+"F0.wireOp",EDGE,"E1.bottom");var subQ7=sQuery(id+"F0.wireOp",EDGE,"E1.right");var subQ8=sQuery(id+"F0.wireOp",EDGE,"E1.top");var subQ9=sQuery(id+"F0.wireOp",EDGE,"E1.left");var subQ10=sQuery(id+"F0.wireOp",EDGE,"E23.filletArc");var subQ11=sQuery(id+"F0.wireOp",EDGE,"E24.filletArc");Q0=makeQuery(id+"F2.boolean.opBoolean","SPLIT",FACE,{"disambiguationData":[TD([makeQuery(id+"F1.opExtrude","SWEPT_FACE",FACE,{"disambiguationData":[OSD([subQ6])]})])],"derivedFrom":makeQuery(id+"F1.opExtrude","CAP_FACE",FACE,{"disambiguationData":[OSD([subQ6,subQ8,subQ9,subQ7,subQ4,subQ3,subQ2,subQ1,subQ0,subQ5,subQ10,subQ11])],"isStart":true})});}
            var sketch = newSketch(context, id + "F16", { "sketchPlane" : qUnion([Q0])});
            skLineSegment(sketch, "E79", {"start": v(0, 100) * mm, "end": v(0, 130) * mm, "construction": true});
            skCircle(sketch, "E80", {"center": v(0, 130) * mm, "radius": 6 * mm});
            skLineSegment(sketch, "E81", {"start": v(-33, 100) * mm, "end": v(-15, 118) * mm});
            skLineSegment(sketch, "E82", {"start": v(-15, 118) * mm, "end": v(-15, 130) * mm});
            skLineSegment(sketch, "E83", {"start": v(33, 100) * mm, "end": v(15, 118) * mm});
            skLineSegment(sketch, "E84", {"start": v(15, 118) * mm, "end": v(15, 130) * mm});
            skArc(sketch, "E85", {"start": v(15, 130) * mm, "mid": v(0, 145) * mm, "end": v(-15, 130) * mm});
            skLineSegment(sketch, "E86", {"start": v(-80, 0) * mm, "end": v(80, 0) * mm, "construction": true});
            skArc(sketch, "E87.MirrorCS", {"start": v(15, -130) * mm, "mid": v(0, -145) * mm, "end": v(-15, -130) * mm});
            skLineSegment(sketch, "E88.MirrorCS", {"start": v(15, -118) * mm, "end": v(15, -130) * mm});
            skLineSegment(sketch, "E89.MirrorCS", {"start": v(33, -100) * mm, "end": v(15, -118) * mm});
            skLineSegment(sketch, "E90.MirrorCS", {"start": v(0, -100) * mm, "end": v(0, -130) * mm, "construction": true});
            skLineSegment(sketch, "E91.MirrorCS", {"start": v(-33, -100) * mm, "end": v(-15, -118) * mm});
            skLineSegment(sketch, "E92.MirrorCS", {"start": v(-15, -118) * mm, "end": v(-15, -130) * mm});
            skCircle(sketch, "E93.MirrorC", {"center": v(0, -130) * mm, "radius": 6 * mm});
            skSolve(sketch);
        }
        {
            var Q0;
            Q0=makeQuery(id+"F16.imprint","IMPRINT",FACE,{"disambiguationData":[TD([[makeQuery(id+"F16.imprint","IMPRINT",EDGE,{"derivedFrom":makeQuery(id+"F1.opExtrude","CAP_EDGE",EDGE,{"disambiguationData":[OSD([sQuery(id+"F0.wireOp",EDGE,"E1.left")])],"isStart":true})}),-1.0]])]});
            var Q1;
            Q1=makeQuery(id+"F16.imprint","IMPRINT",FACE,{"disambiguationData":[TD([[makeQuery(id+"F16.imprint","IMPRINT",EDGE,{"derivedFrom":sQuery(id+"F16.wireOp",EDGE,"E80")}),-1.0]])]});
            var Q2;
            Q2=makeQuery(id+"F16.imprint","IMPRINT",FACE,{"disambiguationData":[TD([[makeQuery(id+"F16.imprint","IMPRINT",EDGE,{"derivedFrom":sQuery(id+"F16.wireOp",EDGE,"E87.MirrorCS")}),-1.0]])]});
            var Q3;
            Q3=makeQuery(id+"F2.opExtrude","CAP_FACE",FACE,{"disambiguationData":[OSD([sQuery(id+"F0.wireOp",EDGE,"E12"),sQuery(id+"F0.wireOp",EDGE,"E13"),sQuery(id+"F0.wireOp",EDGE,"E14"),sQuery(id+"F0.wireOp",EDGE,"E15"),sQuery(id+"F0.wireOp",EDGE,"E17.filletArc"),sQuery(id+"F0.wireOp",EDGE,"E18.filletArc"),sQuery(id+"F0.wireOp",EDGE,"E19.filletArc"),sQuery(id+"F0.wireOp",EDGE,"E20.filletArc"),sQuery(id+"F0.wireOp",EDGE,"E25.0"),sQuery(id+"F0.wireOp",EDGE,"E25.1"),sQuery(id+"F0.wireOp",EDGE,"E25.2"),sQuery(id+"F0.wireOp",EDGE,"E25.3"),sQuery(id+"F0.wireOp",EDGE,"E25.4"),sQuery(id+"F0.wireOp",EDGE,"E25.5"),sQuery(id+"F0.wireOp",EDGE,"E25.6"),sQuery(id+"F0.wireOp",EDGE,"E25.7")])],"isStart":false});
            extrude(context, id + "F17", {"entities" : qUnion([Q0, Q1, Q2]), "endBound" : BoundingType.UP_TO_SURFACE, "endBoundEntityFace" : qUnion([Q3]), "depth" : 25 * mm});
        }
    });
